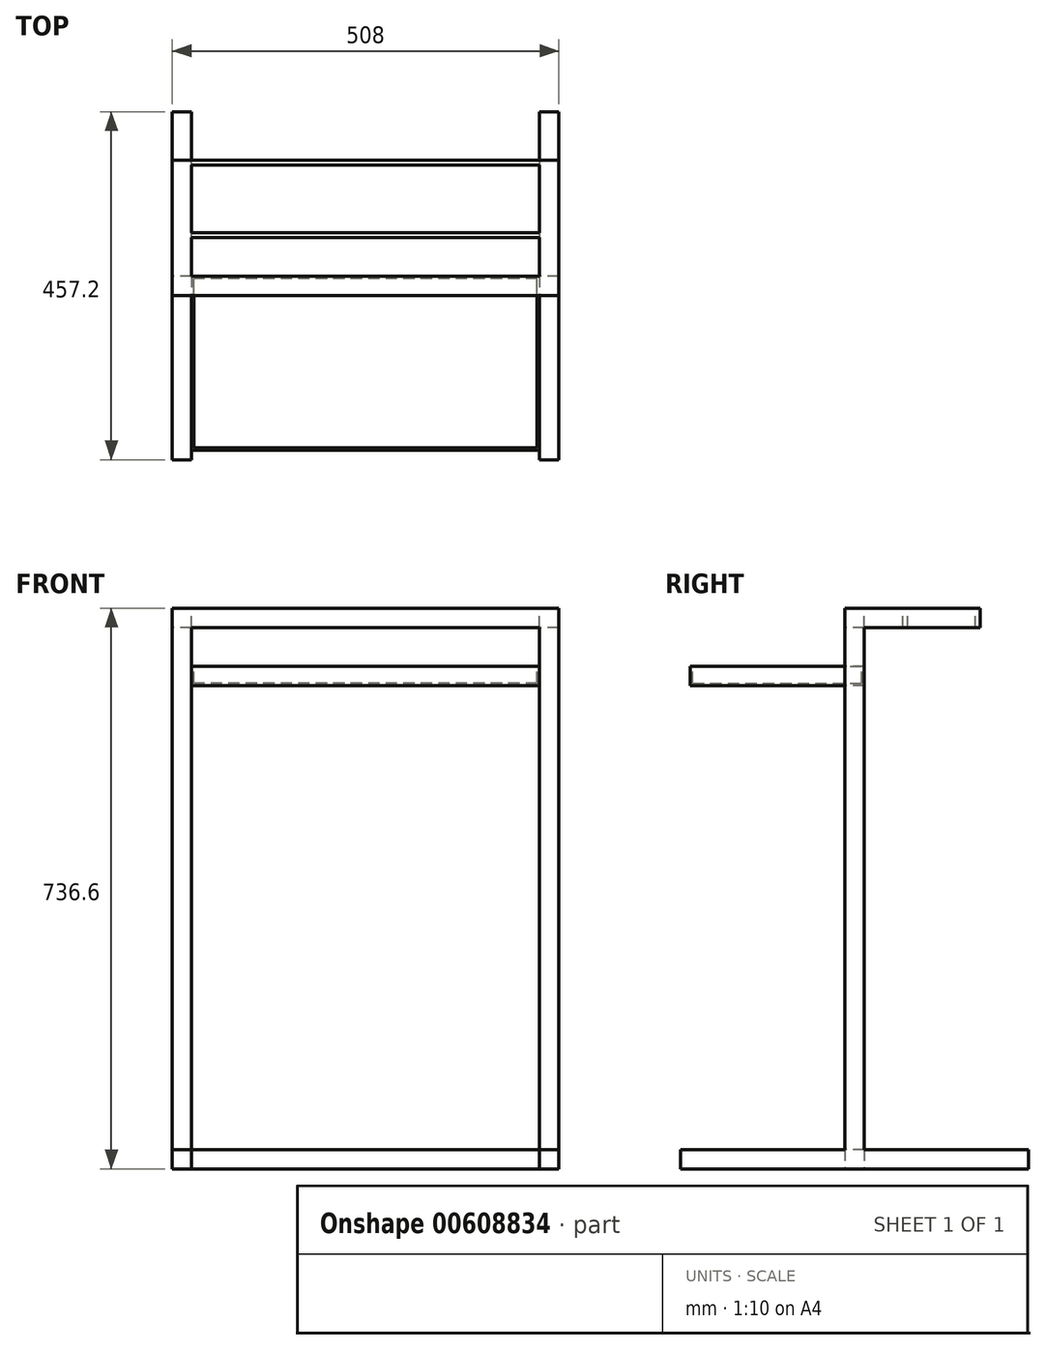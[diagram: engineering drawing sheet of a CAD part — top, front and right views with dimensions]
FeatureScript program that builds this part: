
annotation { "Feature Type Name" : "Feature", "Feature Type Description" : "" }
export const myFeature = defineFeature(function(context is Context, id is Id, definition is map)
    precondition{}
    {
        {
            var Q0;
            Q0=qCreatedBy(makeId("Top.planeOp"),FACE);
            var sketch = newSketch(context, id + "F0", { "sketchPlane" : qUnion([Q0])});
            skLineSegment(sketch, "E0.bottom", {"start": v(0, 0) * mm, "end": v(25.4, 0) * mm});
            skLineSegment(sketch, "E0.top", {"start": v(0, 457.2) * mm, "end": v(25.4, 457.2) * mm});
            skLineSegment(sketch, "E0.left", {"start": v(0, 0) * mm, "end": v(0, 457.2) * mm});
            skLineSegment(sketch, "E0.right", {"start": v(25.4, 0) * mm, "end": v(25.4, 457.2) * mm});
            skLineSegment(sketch, "E1.bottom", {"start": v(482.6, 457.2) * mm, "end": v(508, 457.2) * mm});
            skLineSegment(sketch, "E1.top", {"start": v(482.6, 0) * mm, "end": v(508, 0) * mm});
            skLineSegment(sketch, "E1.left", {"start": v(482.6, 457.2) * mm, "end": v(482.6, 0) * mm});
            skLineSegment(sketch, "E1.right", {"start": v(508, 457.2) * mm, "end": v(508, 0) * mm});
            skLineSegment(sketch, "E2.bottom", {"start": v(25.4, 241.3) * mm, "end": v(482.6, 241.3) * mm});
            skLineSegment(sketch, "E2.top", {"start": v(25.4, 215.9) * mm, "end": v(482.6, 215.9) * mm});
            skLineSegment(sketch, "E2.left", {"start": v(25.4, 241.3) * mm, "end": v(25.4, 215.9) * mm});
            skLineSegment(sketch, "E2.right", {"start": v(482.6, 241.3) * mm, "end": v(482.6, 215.9) * mm});
            skSolve(sketch);
        }
        {
            var Q0;
            Q0 = qSketchRegion(id + "F0", true);
            extrude(context, id + "F1", {"entities" : qUnion([Q0]), "depth" : 25.4 * mm, "offsetDistance" : 25.4 * mm});
        }
        {
            var Q0;
            Q0=makeQuery(id+"F1.opExtrude","CAP_FACE",FACE,{"disambiguationData":[OSD([sQuery(id+"F0.wireOp",EDGE,"E0.bottom"),sQuery(id+"F0.wireOp",EDGE,"E0.top"),sQuery(id+"F0.wireOp",EDGE,"E0.left"),sQuery(id+"F0.wireOp",EDGE,"E0.right"),sQuery(id+"F0.wireOp",EDGE,"E1.bottom"),sQuery(id+"F0.wireOp",EDGE,"E1.top"),sQuery(id+"F0.wireOp",EDGE,"E1.left"),sQuery(id+"F0.wireOp",EDGE,"E1.right"),sQuery(id+"F0.wireOp",EDGE,"E2.bottom"),sQuery(id+"F0.wireOp",EDGE,"E2.top")])],"isStart":false});
            var sketch = newSketch(context, id + "F2", { "sketchPlane" : qUnion([Q0])});
            skLineSegment(sketch, "E3.bottom", {"start": v(25.4, 241.3) * mm, "end": v(0, 241.3) * mm});
            skLineSegment(sketch, "E3.top", {"start": v(25.4, 215.9) * mm, "end": v(0, 215.9) * mm});
            skLineSegment(sketch, "E3.left", {"start": v(25.4, 241.3) * mm, "end": v(25.4, 215.9) * mm});
            skLineSegment(sketch, "E3.right", {"start": v(0, 241.3) * mm, "end": v(0, 215.9) * mm});
            skLineSegment(sketch, "E4.bottom", {"start": v(482.6, 241.3) * mm, "end": v(508, 241.3) * mm});
            skLineSegment(sketch, "E4.top", {"start": v(482.6, 215.9) * mm, "end": v(508, 215.9) * mm});
            skLineSegment(sketch, "E4.left", {"start": v(482.6, 241.3) * mm, "end": v(482.6, 215.9) * mm});
            skLineSegment(sketch, "E4.right", {"start": v(508, 241.3) * mm, "end": v(508, 215.9) * mm});
            skSolve(sketch);
        }
        {
            var Q0;
            Q0 = qSketchRegion(id + "F2", true);
            extrude(context, id + "F3", {"entities" : qUnion([Q0]), "operationType" : NewBodyOperationType.ADD, "depth" : 711.2 * mm, "offsetDistance" : 25.4 * mm});
        }
        {
            var Q0;
            Q0=makeQuery(id+"F3.opExtrude","CAP_FACE",FACE,{"disambiguationData":[OSD([sQuery(id+"F2.wireOp",EDGE,"E3.bottom"),sQuery(id+"F2.wireOp",EDGE,"E3.top"),sQuery(id+"F2.wireOp",EDGE,"E3.left"),sQuery(id+"F2.wireOp",EDGE,"E3.right")])],"isStart":false});
            var sketch = newSketch(context, id + "F4", { "sketchPlane" : qUnion([Q0])});
            skLineSegment(sketch, "E5.bottom", {"start": v(0, 241.3) * mm, "end": v(25.4, 241.3) * mm});
            skLineSegment(sketch, "E5.top", {"start": v(0, 393.7) * mm, "end": v(25.4, 393.7) * mm});
            skLineSegment(sketch, "E5.left", {"start": v(0, 241.3) * mm, "end": v(0, 393.7) * mm});
            skLineSegment(sketch, "E5.right", {"start": v(25.4, 241.3) * mm, "end": v(25.4, 393.7) * mm});
            skLineSegment(sketch, "E6.bottom", {"start": v(508, 393.7) * mm, "end": v(482.6, 393.7) * mm});
            skLineSegment(sketch, "E6.top", {"start": v(508, 241.3) * mm, "end": v(482.6, 241.3) * mm});
            skLineSegment(sketch, "E6.left", {"start": v(508, 393.7) * mm, "end": v(508, 241.3) * mm});
            skLineSegment(sketch, "E6.right", {"start": v(482.6, 393.7) * mm, "end": v(482.6, 241.3) * mm});
            skLineSegment(sketch, "E7.bottom", {"start": v(25.4, 393.7) * mm, "end": v(482.6, 393.7) * mm});
            skLineSegment(sketch, "E7.top", {"start": v(25.4, 387.35) * mm, "end": v(482.6, 387.35) * mm});
            skLineSegment(sketch, "E7.left", {"start": v(25.4, 393.7) * mm, "end": v(25.4, 387.35) * mm});
            skLineSegment(sketch, "E7.right", {"start": v(482.6, 393.7) * mm, "end": v(482.6, 387.35) * mm});
            skLineSegment(sketch, "E8.bottom", {"start": v(25.4, 349.25) * mm, "end": v(482.6, 349.25) * mm});
            skLineSegment(sketch, "E8.top", {"start": v(25.4, 342.9) * mm, "end": v(482.6, 342.9) * mm});
            skLineSegment(sketch, "E8.left", {"start": v(25.4, 349.25) * mm, "end": v(25.4, 342.9) * mm});
            skLineSegment(sketch, "E8.right", {"start": v(482.6, 349.25) * mm, "end": v(482.6, 342.9) * mm});
            skLineSegment(sketch, "E9.bottom", {"start": v(25.4, 298.45) * mm, "end": v(482.6, 298.45) * mm});
            skLineSegment(sketch, "E9.top", {"start": v(25.4, 292.1) * mm, "end": v(482.6, 292.1) * mm});
            skLineSegment(sketch, "E9.left", {"start": v(25.4, 298.45) * mm, "end": v(25.4, 292.1) * mm});
            skLineSegment(sketch, "E9.right", {"start": v(482.6, 298.45) * mm, "end": v(482.6, 292.1) * mm});
            skSolve(sketch);
        }
        {
            var Q0;
            Q0 = qSketchRegion(id + "F4", true);
            extrude(context, id + "F5", {"entities" : qUnion([Q0]), "operationType" : NewBodyOperationType.ADD, "oppositeDirection" : true, "depth" : 25.4 * mm, "offsetDistance" : 25.4 * mm});
        }
        {
            var Q0;
            Q0=makeQuery(id+"F5.boolean.opBoolean","MERGE",FACE,{"derivedFrom":[makeQuery(id+"F3.opExtrude","SWEPT_FACE",FACE,{"disambiguationData":[OSD([sQuery(id+"F2.wireOp",EDGE,"E3.left")])]}),makeQuery(id+"F5.opExtrude","SWEPT_FACE",FACE,{"disambiguationData":[OSD([sQuery(id+"F4.wireOp",EDGE,"E5.right")])]}),makeQuery(id+"F5.opExtrude","SWEPT_FACE",FACE,{"disambiguationData":[OSD([sQuery(id+"F4.wireOp",EDGE,"c148c0fa-b51a-42b4-bf1a-5af334bdcc580.MirrorCS")])]})]});
            var sketch = newSketch(context, id + "F6", { "sketchPlane" : qUnion([Q0])});
            skLineSegment(sketch, "E10.bottom", {"start": v(241.3, 660.4) * mm, "end": v(12.7, 660.4) * mm});
            skLineSegment(sketch, "E10.top", {"start": v(241.3, 635) * mm, "end": v(12.7, 635) * mm});
            skLineSegment(sketch, "E10.left", {"start": v(241.3, 660.4) * mm, "end": v(241.3, 635) * mm});
            skLineSegment(sketch, "E10.right", {"start": v(12.7, 660.4) * mm, "end": v(12.7, 635) * mm});
            skLineSegment(sketch, "E11.bottom", {"start": v(241.3, 711.2) * mm, "end": v(215.9, 711.2) * mm});
            skLineSegment(sketch, "E11.top", {"start": v(241.3, 736.6) * mm, "end": v(215.9, 736.6) * mm});
            skLineSegment(sketch, "E11.left", {"start": v(241.3, 711.2) * mm, "end": v(241.3, 736.6) * mm});
            skLineSegment(sketch, "E11.right", {"start": v(215.9, 711.2) * mm, "end": v(215.9, 736.6) * mm});
            skSolve(sketch);
        }
        {
            var Q0;
            Q0 = qSketchRegion(id + "F6", true);
            var Q1;
            Q1=makeQuery(id+"F5.boolean.opBoolean","MERGE",FACE,{"derivedFrom":[makeQuery(id+"F3.opExtrude","SWEPT_FACE",FACE,{"disambiguationData":[OSD([sQuery(id+"F2.wireOp",EDGE,"E4.left")])]}),makeQuery(id+"F5.opExtrude","SWEPT_FACE",FACE,{"disambiguationData":[OSD([sQuery(id+"F4.wireOp",EDGE,"E6.right")])]}),makeQuery(id+"F5.opExtrude","SWEPT_FACE",FACE,{"disambiguationData":[OSD([sQuery(id+"F4.wireOp",EDGE,"9a7f09e2-2c52-468b-b702-e137052730df0.MirrorCS")])]})]});
            extrude(context, id + "F7", {"entities" : qUnion([Q0]), "operationType" : NewBodyOperationType.ADD, "endBound" : BoundingType.UP_TO_SURFACE, "depth" : 25.4 * mm, "endBoundEntityFace" : qUnion([Q1]), "offsetDistance" : 25.4 * mm});
        }
        {
            var Q0;
            Q0=makeQuery(id+"F7.opExtrude","SWEPT_FACE",FACE,{"disambiguationData":[OSD([sQuery(id+"F6.wireOp",EDGE,"E10.bottom")])]});
            var sketch = newSketch(context, id + "F8", { "sketchPlane" : qUnion([Q0])});
            skLineSegment(sketch, "E12.bottom", {"start": v(479.42, 15.87) * mm, "end": v(28.57, 15.87) * mm});
            skLineSegment(sketch, "E12.top", {"start": v(479.42, 238.13) * mm, "end": v(28.57, 238.13) * mm});
            skLineSegment(sketch, "E12.left", {"start": v(479.42, 15.87) * mm, "end": v(479.42, 238.13) * mm});
            skLineSegment(sketch, "E12.right", {"start": v(28.57, 15.87) * mm, "end": v(28.57, 238.13) * mm});
            skSolve(sketch);
        }
        {
            var Q0;
            Q0=makeQuery(id+"F8.imprint","IMPRINT",FACE,{"disambiguationData":[TD([[makeQuery(id+"F8.imprint","IMPRINT",EDGE,{"derivedFrom":sQuery(id+"F8.wireOp",EDGE,"E12.bottom")}),-1.0]])]});
            extrude(context, id + "F9", {"entities" : qUnion([Q0]), "operationType" : NewBodyOperationType.REMOVE, "oppositeDirection" : true, "depth" : 22.22 * mm, "offsetDistance" : 25.4 * mm});
        }
    });
